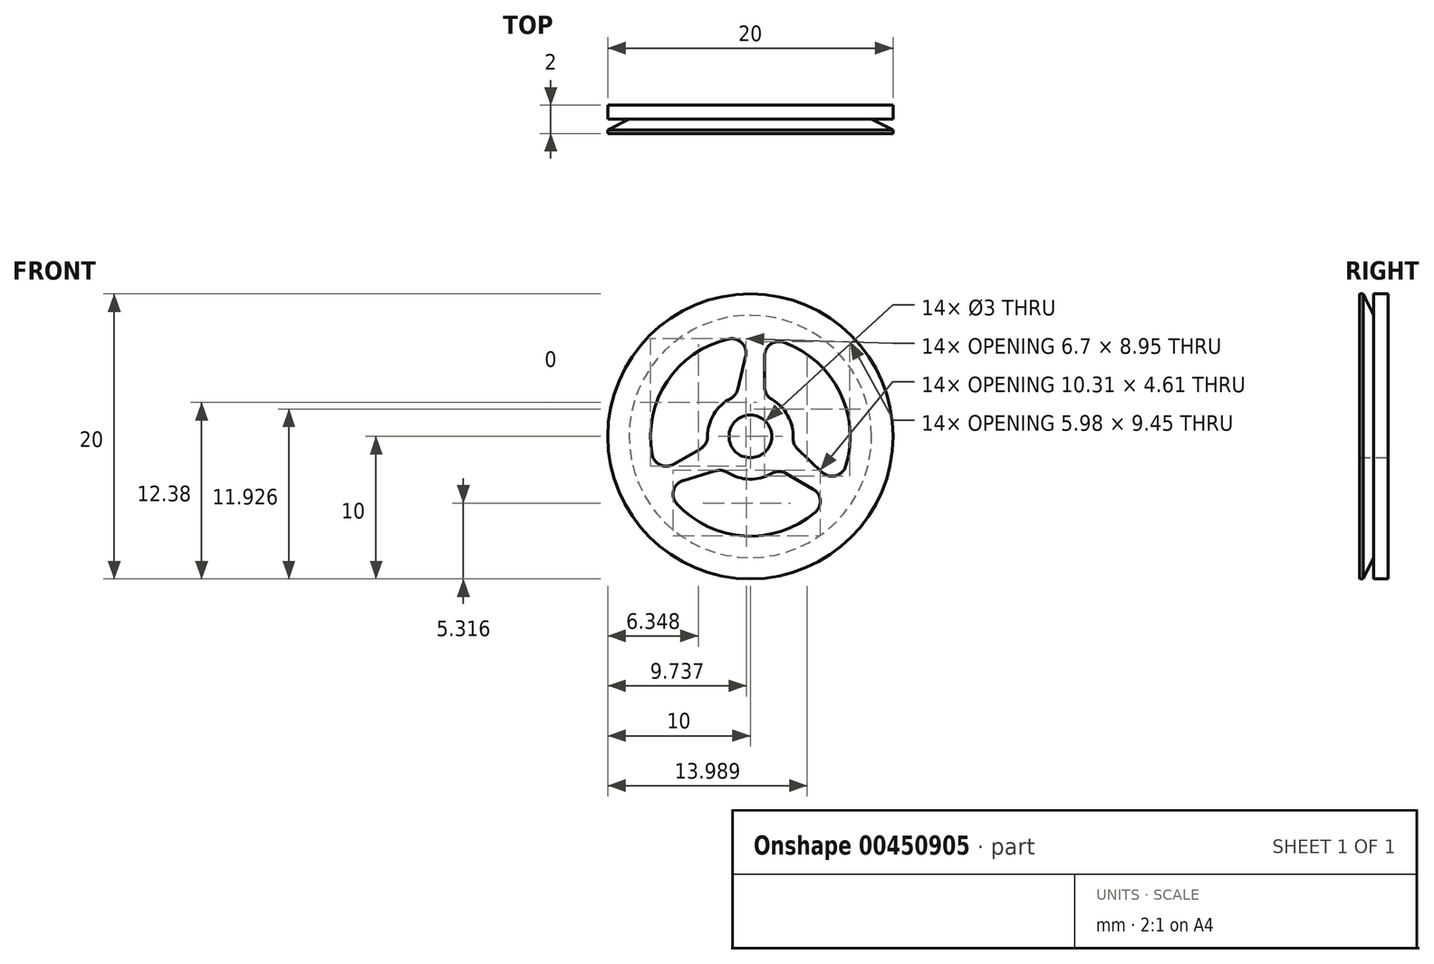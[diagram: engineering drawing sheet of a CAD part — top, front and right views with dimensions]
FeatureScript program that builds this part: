
annotation { "Feature Type Name" : "Feature", "Feature Type Description" : "" }
export const myFeature = defineFeature(function(context is Context, id is Id, definition is map)
    precondition{}
    {
        {
            var Q0;
            Q0=qCreatedBy(makeId("Front.planeOp"),FACE);
            var sketch = newSketch(context, id + "F0", { "sketchPlane" : qUnion([Q0])});
            skCircle(sketch, "E0", {"center": v(0, 0) * mm, "radius": 10 * mm});
            skArc(sketch, "E1.0", {"start": v(-1.52, 6.83) * mm, "mid": v(-5.84, 3.86) * mm, "end": v(-6.88, -1.28) * mm});
            skArc(sketch, "E2", {"start": v(3, -0.12) * mm, "mid": v(2.63, 1.45) * mm, "end": v(1.5, 2.6) * mm});
            skCircle(sketch, "E3", {"center": v(0, 0) * mm, "radius": 1.5 * mm});
            skLineSegment(sketch, "E4.0", {"start": v(0.7, 9.97) * mm, "end": v(0.7, 9.95) * mm});
            skLineSegment(sketch, "E5.0", {"start": v(1, 10) * mm, "end": v(1, 9.95) * mm});
            skLineSegment(sketch, "E6.trimOffspring", {"start": v(-0.33, 5.62) * mm, "end": v(-0.88, 3.3) * mm});
            skLineSegment(sketch, "E7.trimOffspring", {"start": v(1, 5.66) * mm, "end": v(1, 3.46) * mm});
            skPoint(sketch, "E8.orphan", {"position": v(0, 10) * mm});
            skLineSegment(sketch, "E9.1.0", {"start": v(-5.4, -1.96) * mm, "end": v(-3.5, -0.87) * mm});
            skLineSegment(sketch, "E9.1.1", {"start": v(-4.7, -3.1) * mm, "end": v(-2.42, -2.42) * mm});
            skLineSegment(sketch, "E9.2.0", {"start": v(4.4, -3.7) * mm, "end": v(2.5, -2.6) * mm});
            skLineSegment(sketch, "E9.2.1", {"start": v(5.04, -2.53) * mm, "end": v(3.3, -0.89) * mm});
            skArc(sketch, "E10.trimOffspring", {"start": v(-5.16, -4.73) * mm, "mid": v(-0.42, -6.99) * mm, "end": v(4.55, -5.32) * mm});
            skArc(sketch, "E11.trimOffspring", {"start": v(6.68, -2.1) * mm, "mid": v(6.26, 3.13) * mm, "end": v(2.33, 6.6) * mm});
            skArc(sketch, "E12.trimOffspring", {"start": v(-1.6, -2.53) * mm, "mid": v(-0.06, -3) * mm, "end": v(1.5, -2.6) * mm});
            skArc(sketch, "E13.trimOffspring", {"start": v(-1.4, 2.66) * mm, "mid": v(-2.57, 1.55) * mm, "end": v(-3, 0) * mm});
            skPoint(sketch, "E14.visualSharp", {"position": v(0, 7) * mm});
            skArc(sketch, "E14.filletArc", {"start": v(-0.33, 5.62) * mm, "mid": v(-0.6, 6.56) * mm, "end": v(-1.52, 6.83) * mm});
            skPoint(sketch, "E15.visualSharp", {"position": v(-1, 2.83) * mm});
            skArc(sketch, "E15.filletArc", {"start": v(-1.4, 2.66) * mm, "mid": v(-1.07, 2.93) * mm, "end": v(-0.88, 3.3) * mm});
            skPoint(sketch, "E16.visualSharp", {"position": v(-2.95, -0.55) * mm});
            skArc(sketch, "E16.filletArc", {"start": v(-3.5, -0.87) * mm, "mid": v(-3.13, -0.5) * mm, "end": v(-3, 0) * mm});
            skPoint(sketch, "E17.visualSharp", {"position": v(-6.5, -2.6) * mm});
            skArc(sketch, "E17.filletArc", {"start": v(-6.88, -1.28) * mm, "mid": v(-6.32, -2) * mm, "end": v(-5.4, -1.96) * mm});
            skPoint(sketch, "E18.visualSharp", {"position": v(-6.06, -3.5) * mm});
            skArc(sketch, "E18.filletArc", {"start": v(-4.7, -3.1) * mm, "mid": v(-5.38, -3.8) * mm, "end": v(-5.16, -4.73) * mm});
            skPoint(sketch, "E19.visualSharp", {"position": v(5.5, -4.33) * mm});
            skArc(sketch, "E19.filletArc", {"start": v(4.55, -5.32) * mm, "mid": v(4.9, -4.47) * mm, "end": v(4.4, -3.7) * mm});
            skPoint(sketch, "E20.visualSharp", {"position": v(6.06, -3.5) * mm});
            skArc(sketch, "E20.filletArc", {"start": v(5.04, -2.53) * mm, "mid": v(5.98, -2.77) * mm, "end": v(6.68, -2.1) * mm});
            skPoint(sketch, "E21.visualSharp", {"position": v(1, 6.93) * mm});
            skArc(sketch, "E21.filletArc", {"start": v(2.33, 6.6) * mm, "mid": v(1.42, 6.47) * mm, "end": v(1, 5.66) * mm});
            skPoint(sketch, "E22.visualSharp", {"position": v(-1.95, -2.28) * mm});
            skArc(sketch, "E22.filletArc", {"start": v(-1.6, -2.53) * mm, "mid": v(-2, -2.39) * mm, "end": v(-2.42, -2.42) * mm});
            skPoint(sketch, "E23.visualSharp", {"position": v(1.95, -2.28) * mm});
            skArc(sketch, "E23.filletArc", {"start": v(2.5, -2.6) * mm, "mid": v(2, -2.46) * mm, "end": v(1.5, -2.6) * mm});
            skPoint(sketch, "E24.visualSharp", {"position": v(1, 2.83) * mm});
            skArc(sketch, "E24.filletArc", {"start": v(1, 3.46) * mm, "mid": v(1.13, 2.96) * mm, "end": v(1.5, 2.6) * mm});
            skPoint(sketch, "E25.visualSharp", {"position": v(2.95, -0.55) * mm});
            skArc(sketch, "E25.filletArc", {"start": v(3, -0.12) * mm, "mid": v(3.07, -0.54) * mm, "end": v(3.3, -0.89) * mm});
            skSolve(sketch);
        }
        {
            var Q0;
            Q0=makeQuery(id+"F0.imprint","IMPRINT",FACE,{"disambiguationData":[TD([[makeQuery(id+"F0.imprint","IMPRINT",EDGE,{"derivedFrom":sQuery(id+"F0.wireOp",EDGE,"E1.0")}),-1.0]])]});
            extrude(context, id + "F1", {"entities" : qUnion([Q0]), "endBound" : BoundingType.SYMMETRIC, "depth" : 2 * mm});
        }
        {
            var Q0;
            Q0=qCreatedBy(makeId("Right.planeOp"),FACE);
            var sketch = newSketch(context, id + "F2", { "sketchPlane" : qUnion([Q0])});
            skLineSegment(sketch, "E26", {"start": v(0, 10) * mm, "end": v(0, 8.5) * mm});
            skLineSegment(sketch, "E27", {"start": v(0, 10) * mm, "end": v(-0.75, 10) * mm});
            skLineSegment(sketch, "E28", {"start": v(-0.75, 10) * mm, "end": v(0, 8.5) * mm});
            skLineSegment(sketch, "E29.MirrorCS", {"start": v(0.75, 10) * mm, "end": v(0, 8.5) * mm});
            skLineSegment(sketch, "E30", {"start": v(0, 0) * mm, "end": v(-2.55, 0) * mm});
            skLineSegment(sketch, "E31", {"start": v(-2.55, 0) * mm, "end": v(5.1, 0) * mm});
            skSolve(sketch);
        }
        {
            var Q0;
            Q0 = qSketchRegion(id + "F2", true);
            var Q1;
            Q1=sQuery(id+"F2.wireOp",EDGE,"E31");
            revolve(context, id + "F3", {"operationType" : NewBodyOperationType.REMOVE, "entities" : qUnion([Q0]), "axis" : qUnion([Q1]), "revolveType" : RevolveType.FULL, "oppositeDirection" : true});
        }
    });
